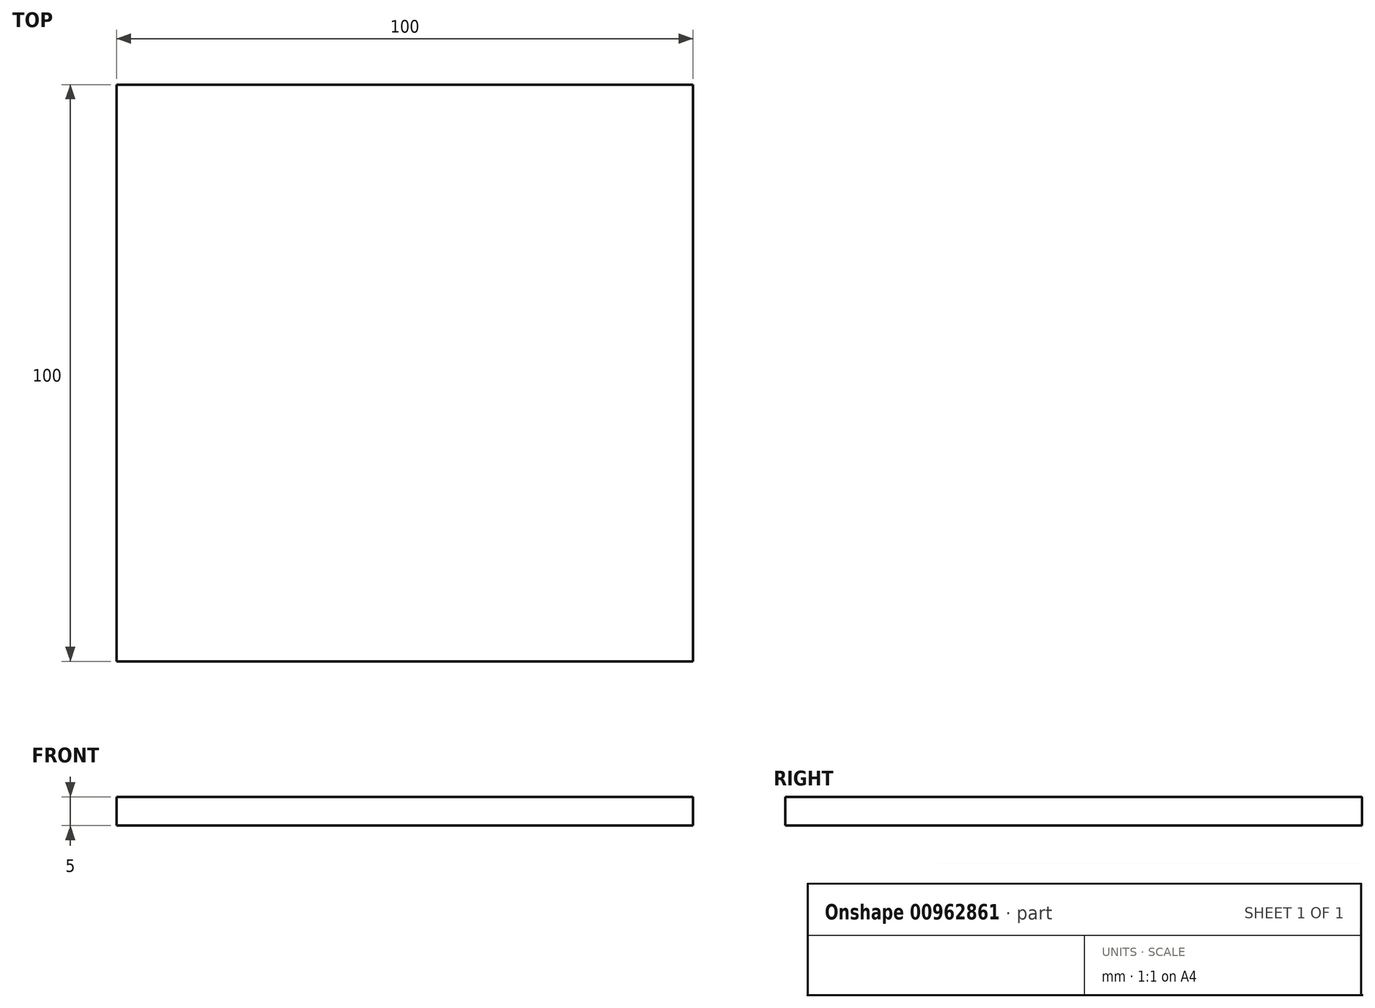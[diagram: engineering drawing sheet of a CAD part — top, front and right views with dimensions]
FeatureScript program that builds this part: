
annotation { "Feature Type Name" : "Feature", "Feature Type Description" : "" }
export const myFeature = defineFeature(function(context is Context, id is Id, definition is map)
    precondition{}
    {
        {
            var Q0;
            Q0=qCreatedBy(makeId("Top.planeOp"),FACE);
            var sketch = newSketch(context, id + "F0", { "sketchPlane" : qUnion([Q0])});
            skLineSegment(sketch, "E0.bottom", {"start": v(50, -50) * mm, "end": v(-50, -50) * mm});
            skLineSegment(sketch, "E0.top", {"start": v(50, 50) * mm, "end": v(-50, 50) * mm});
            skLineSegment(sketch, "E0.left", {"start": v(50, -50) * mm, "end": v(50, 50) * mm});
            skLineSegment(sketch, "E0.right", {"start": v(-50, -50) * mm, "end": v(-50, 50) * mm});
            skPoint(sketch, "E0.middle", {"position": v(0, 0) * mm});
            skSolve(sketch);
        }
        {
            var Q0;
            Q0 = qSketchRegion(id + "F0", true);
            extrude(context, id + "F1", {"entities" : qUnion([Q0]), "depth" : 5 * mm, "offsetDistance" : 25 * mm});
        }
    });
